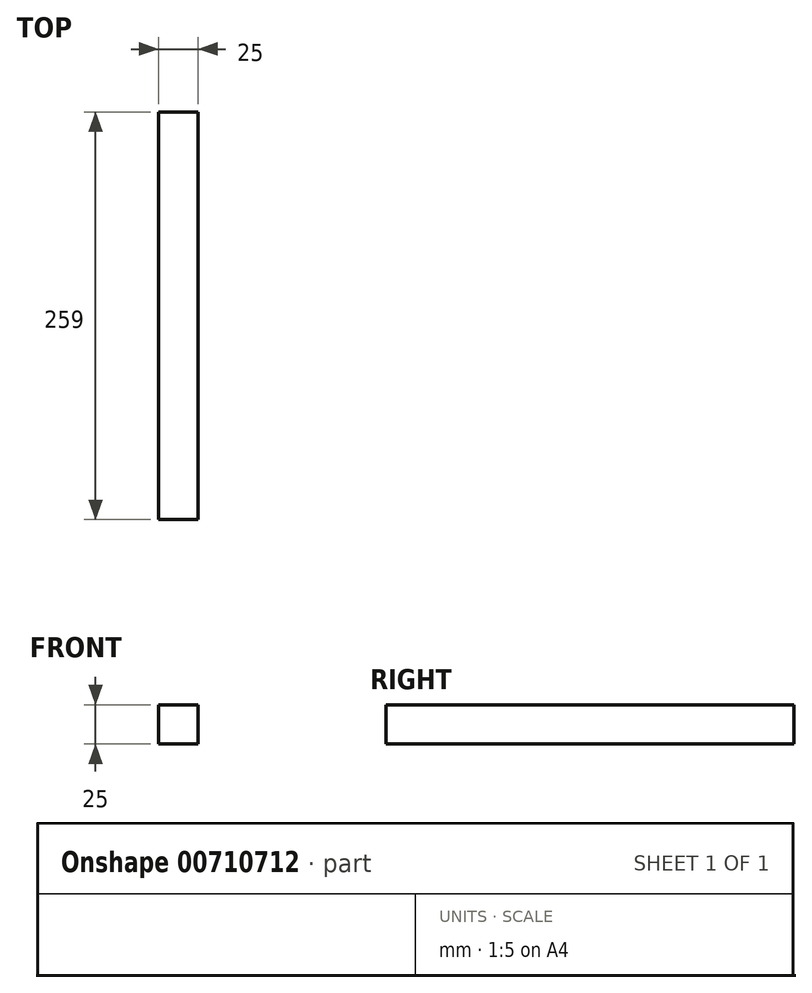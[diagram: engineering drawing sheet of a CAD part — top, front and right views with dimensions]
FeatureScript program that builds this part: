
annotation { "Feature Type Name" : "Feature", "Feature Type Description" : "" }
export const myFeature = defineFeature(function(context is Context, id is Id, definition is map)
    precondition{}
    {
        {
            assignVariable(context, id + "F0", {"name" : "l", "anyValue" : 259});
        }
        {
            var Q0;
            Q0=qCreatedBy(makeId("Front.planeOp"),FACE);
            var sketch = newSketch(context, id + "F1", { "sketchPlane" : qUnion([Q0])});
            skLineSegment(sketch, "E0.bottom", {"start": v(0, 0) * mm, "end": v(25, 0) * mm});
            skLineSegment(sketch, "E0.top", {"start": v(0, 25) * mm, "end": v(25, 25) * mm});
            skLineSegment(sketch, "E0.left", {"start": v(0, 0) * mm, "end": v(0, 25) * mm});
            skLineSegment(sketch, "E0.right", {"start": v(25, 0) * mm, "end": v(25, 25) * mm});
            skSolve(sketch);
        }
        {
            var Q0;
            Q0=qSketchRegion(id+"F1",true);
            extrude(context, id + "F2", {"entities" : qUnion([Q0]), "depth" : (getVariable(context, 'l')) * mm, "offsetDistance" : 25 * mm});
        }
    });
